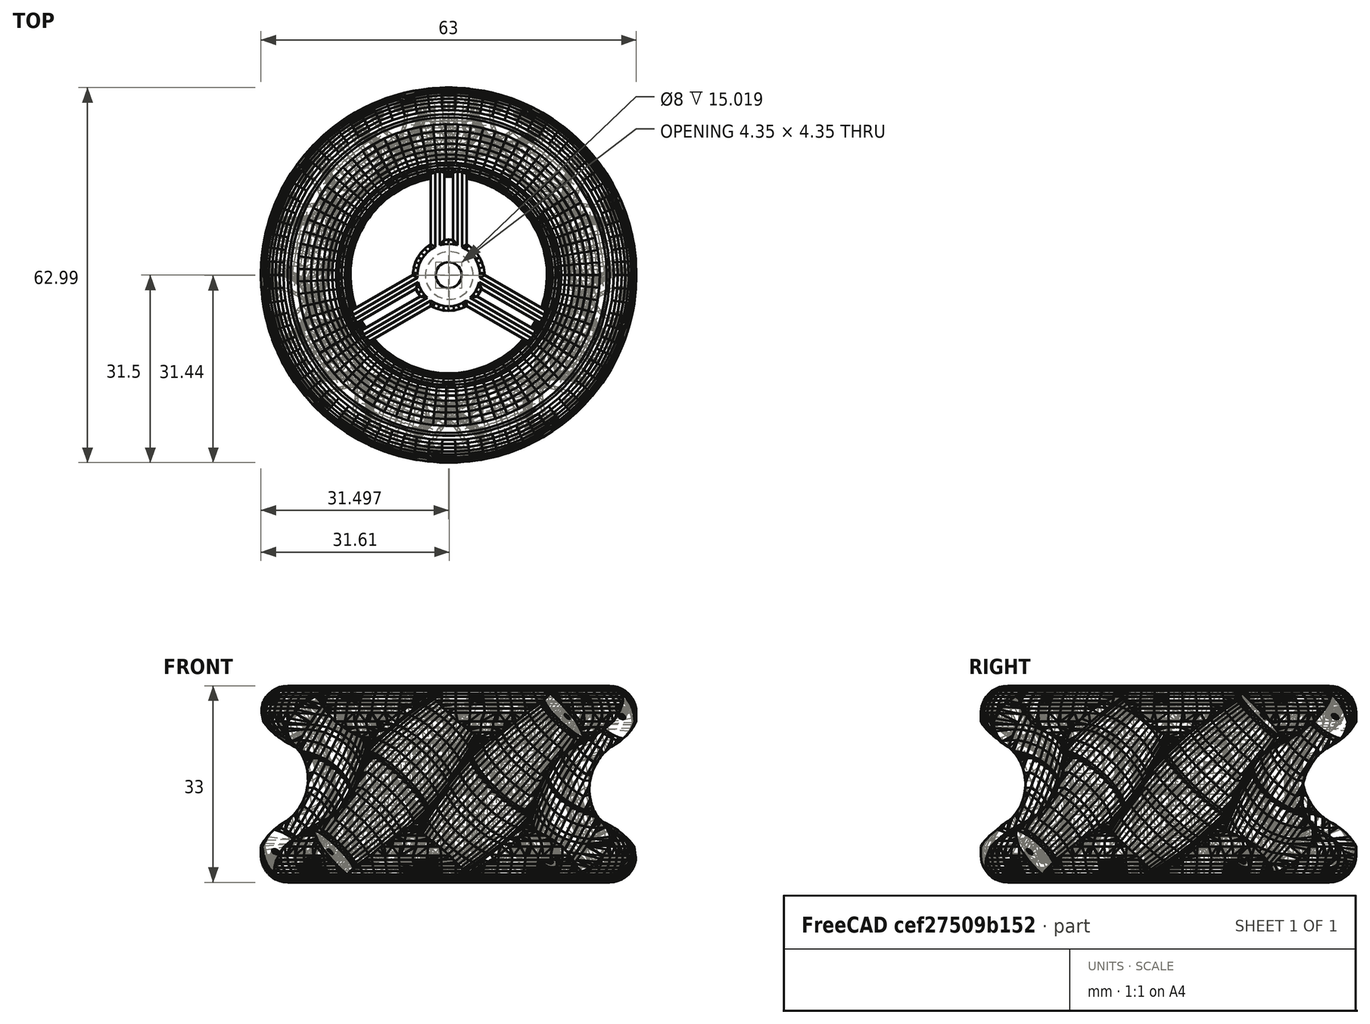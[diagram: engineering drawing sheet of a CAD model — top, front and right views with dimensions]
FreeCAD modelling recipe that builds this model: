
FCSTD DOCUMENT  (FreeCAD 0.17R13522 (Git))
Label: Body_Left
License: All rights reserved
LicenseURL: http://en.wikipedia.org/wiki/All_rights_reserved
objects: Part::Feature×2, Part::FeaturePython×1, Part::Cylinder×1, Part::Cut×1, Mesh::Feature×1
note: 5 computed .brp shape members not serialized (recipe doc carries the construction recipe); baked Part::Feature solids carry a one-line shape summary decoded from their .brp

FEATURE [Part::Feature] Body_Left001_solid  label="Body_Left001 (Solid)"
  shape: large baked B-rep (31 MB .brp); summary skipped
FEATURE [Part::Feature] Body_Left001_solid001  label="Body_Left001 (Solid)001"
  shape: large baked B-rep (30 MB .brp); summary skipped
FEATURE [Part::FeaturePython] Scale  # Draft clone (typed FeaturePython)
  Fuse = false
  Objects = -> [Body_Left001_solid001]
  Placement = pos=(-71.7462,-6.51555,-0.595882) rot=(0,0,1;0rad)
  Scale = (1.5,1.5,1.5)
FEATURE [Part::Cylinder] Cylinder  label="Cilindro"
  Angle = 360
  AttacherType = Attacher::AttachEngine3D
  Height = 20
  Placement = pos=(29.5,26.5,-5) rot=(0,0,1;0rad)
  Radius = 4
FEATURE [Part::Cut] Cut
  Base = -> Scale
  Tool = -> Cylinder
FEATURE [Mesh::Feature] enganche
  Placement = pos=(29.5,26.5,-5) rot=(0,0,1;0rad)
